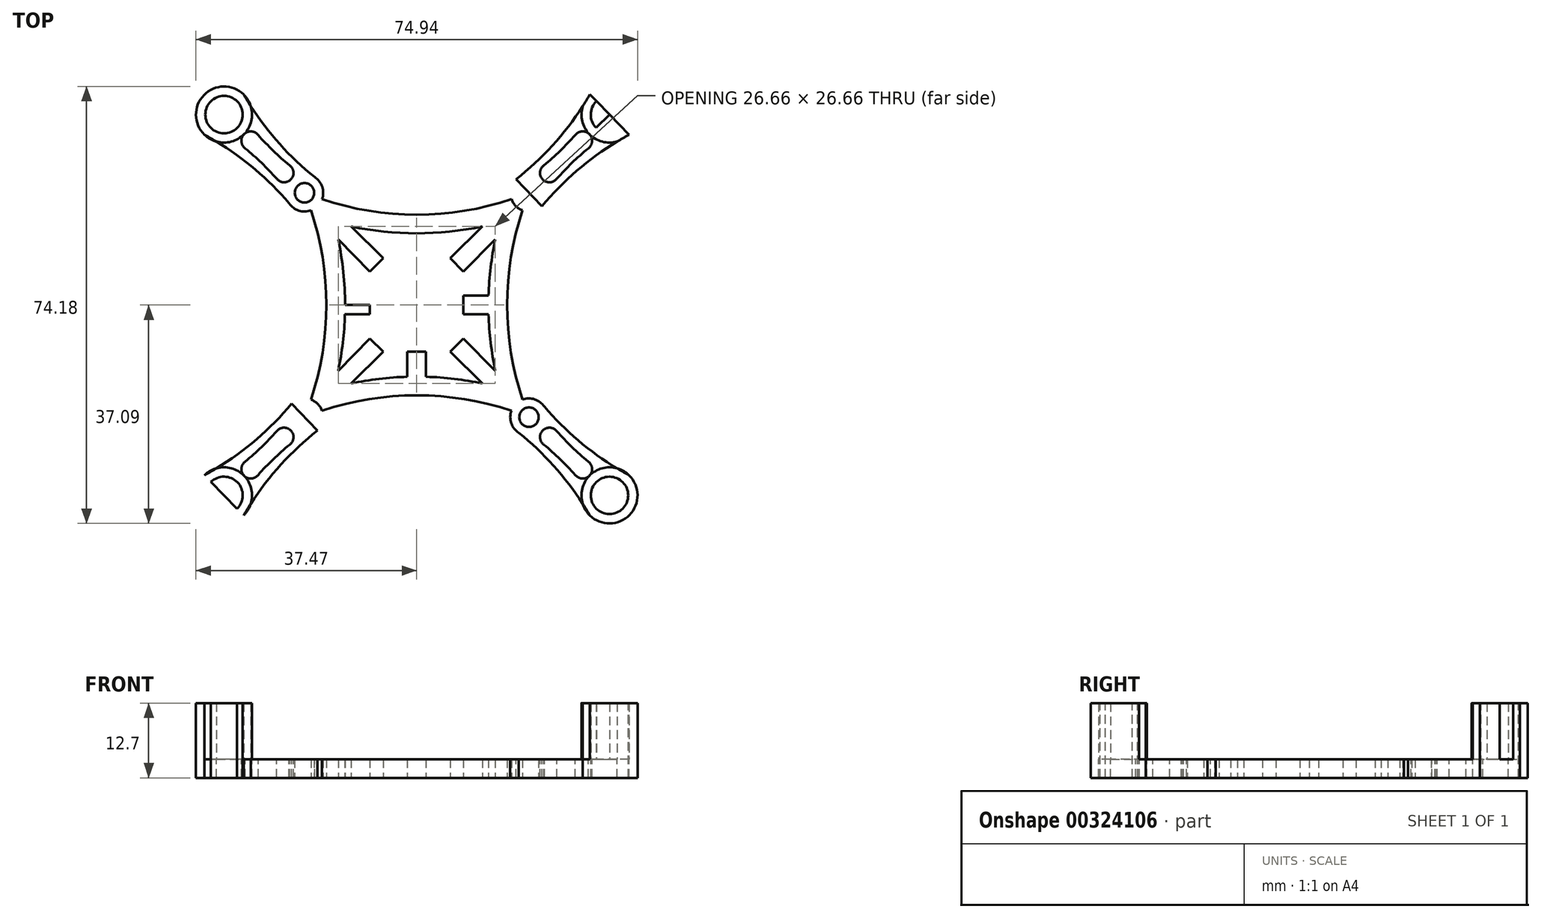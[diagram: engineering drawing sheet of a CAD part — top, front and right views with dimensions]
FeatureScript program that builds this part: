
annotation { "Feature Type Name" : "Feature", "Feature Type Description" : "" }
export const myFeature = defineFeature(function(context is Context, id is Id, definition is map)
    precondition{}
    {
        {
            var Q0;
            Q0=qCreatedBy(makeId("Top.planeOp"),FACE);
            var sketch = newSketch(context, id + "F0", { "sketchPlane" : qUnion([Q0])});
            skPoint(sketch, "E0.middle", {"position": v(0, 0) * mm});
            skLineSegment(sketch, "E1.bottom", {"start": v(-7.94, 7.94) * mm, "end": v(7.94, 7.94) * mm});
            skLineSegment(sketch, "E1.top", {"start": v(-7.94, -7.94) * mm, "end": v(7.94, -7.94) * mm});
            skLineSegment(sketch, "E1.left", {"start": v(-7.94, 7.94) * mm, "end": v(-7.94, -7.94) * mm});
            skLineSegment(sketch, "E1.right", {"start": v(7.94, 7.94) * mm, "end": v(7.94, -7.94) * mm});
            skCircle(sketch, "E2", {"center": v(-19.05, 19.05) * mm, "radius": 3.18 * mm});
            skCircle(sketch, "E3", {"center": v(-19.05, 19.05) * mm, "radius": 1.65 * mm});
            skCircle(sketch, "E4.MirrorC", {"center": v(19.05, 19.05) * mm, "radius": 3.18 * mm});
            skCircle(sketch, "E5.MirrorC", {"center": v(19.05, 19.05) * mm, "radius": 1.65 * mm});
            skCircle(sketch, "E6.MirrorC", {"center": v(-19.05, -19.05) * mm, "radius": 3.18 * mm});
            skCircle(sketch, "E7.MirrorC", {"center": v(-19.05, -19.05) * mm, "radius": 1.65 * mm});
            skCircle(sketch, "E8.MirrorC", {"center": v(19.05, -19.05) * mm, "radius": 3.18 * mm});
            skCircle(sketch, "E9.MirrorC", {"center": v(19.05, -19.05) * mm, "radius": 1.65 * mm});
            skArc(sketch, "E10", {"start": v(-19.05, 19.05) * mm, "mid": v(0, 15.34) * mm, "end": v(19.05, 19.05) * mm});
            skArc(sketch, "E11", {"start": v(19.05, 19.05) * mm, "mid": v(15.34, 0) * mm, "end": v(19.05, -19.05) * mm});
            skArc(sketch, "E12.MirrorCS", {"start": v(19.05, -19.05) * mm, "mid": v(15.34, 0) * mm, "end": v(19.05, 19.05) * mm});
            skArc(sketch, "E13.MirrorCS", {"start": v(19.05, 19.05) * mm, "mid": v(0, 15.34) * mm, "end": v(-19.05, 19.05) * mm});
            skArc(sketch, "E14.MirrorCS", {"start": v(-19.05, -19.05) * mm, "mid": v(-15.34, 0) * mm, "end": v(-19.05, 19.05) * mm});
            skArc(sketch, "E15.MirrorCS", {"start": v(19.05, -19.05) * mm, "mid": v(0, -15.34) * mm, "end": v(-19.05, -19.05) * mm});
            skArc(sketch, "E16.0", {"start": v(14.02, 14.02) * mm, "mid": v(0, 12.17) * mm, "end": v(-14.02, 14.02) * mm});
            skArc(sketch, "E16.1", {"start": v(14.02, 14.02) * mm, "mid": v(12.17, 0) * mm, "end": v(14.02, -14.02) * mm});
            skArc(sketch, "E16.2", {"start": v(14.02, -14.02) * mm, "mid": v(0, -12.17) * mm, "end": v(-14.02, -14.02) * mm});
            skArc(sketch, "E16.3", {"start": v(-14.02, -14.02) * mm, "mid": v(-12.17, 0) * mm, "end": v(-14.02, 14.02) * mm});
            skLineSegment(sketch, "E17.bottom", {"start": v(0, 7.94) * mm, "end": v(-1.59, 7.94) * mm});
            skLineSegment(sketch, "E17.top", {"start": v(0, 13.02) * mm, "end": v(-1.59, 13.02) * mm});
            skLineSegment(sketch, "E17.left", {"start": v(0, 7.94) * mm, "end": v(0, 13.02) * mm});
            skLineSegment(sketch, "E17.right", {"start": v(-1.59, 7.94) * mm, "end": v(-1.59, 13.02) * mm});
            skLineSegment(sketch, "E18.MirrorCS", {"start": v(-1.59, -7.94) * mm, "end": v(-1.59, -13.02) * mm});
            skLineSegment(sketch, "E19.MirrorCS", {"start": v(0, -7.94) * mm, "end": v(0, -13.02) * mm});
            skLineSegment(sketch, "E20.MirrorCS", {"start": v(0, -13.02) * mm, "end": v(-1.59, -13.02) * mm});
            skLineSegment(sketch, "E21.MirrorCS", {"start": v(0, -13.02) * mm, "end": v(1.59, -13.02) * mm});
            skLineSegment(sketch, "E22.MirrorCS", {"start": v(1.59, -7.94) * mm, "end": v(1.59, -13.02) * mm});
            skLineSegment(sketch, "E23.MirrorCS", {"start": v(7.94, -7.94) * mm, "end": v(-7.94, -7.94) * mm});
            skLineSegment(sketch, "E24.MirrorCS", {"start": v(1.59, 7.94) * mm, "end": v(1.59, 13.02) * mm});
            skLineSegment(sketch, "E25.MirrorCS", {"start": v(0, 13.02) * mm, "end": v(1.59, 13.02) * mm});
            skLineSegment(sketch, "E26.bottom", {"start": v(-7.94, 0) * mm, "end": v(-13.02, 0) * mm});
            skLineSegment(sketch, "E26.top", {"start": v(-7.94, 1.59) * mm, "end": v(-13.02, 1.59) * mm});
            skLineSegment(sketch, "E26.left", {"start": v(-7.94, 0) * mm, "end": v(-7.94, 1.59) * mm});
            skLineSegment(sketch, "E26.right", {"start": v(-13.02, 0) * mm, "end": v(-13.02, 1.59) * mm});
            skLineSegment(sketch, "E27.MirrorCS", {"start": v(7.94, 1.59) * mm, "end": v(13.02, 1.59) * mm});
            skLineSegment(sketch, "E28.MirrorCS", {"start": v(13.02, 0) * mm, "end": v(13.02, 1.59) * mm});
            skLineSegment(sketch, "E29.MirrorCS", {"start": v(7.94, 0) * mm, "end": v(13.02, 0) * mm});
            skLineSegment(sketch, "E30.MirrorCS", {"start": v(-13.02, 0) * mm, "end": v(-13.02, -1.59) * mm});
            skLineSegment(sketch, "E31.MirrorCS", {"start": v(-7.94, -1.59) * mm, "end": v(-13.02, -1.59) * mm});
            skLineSegment(sketch, "E32.MirrorCS", {"start": v(7.94, -1.59) * mm, "end": v(13.02, -1.59) * mm});
            skLineSegment(sketch, "E33.MirrorCS", {"start": v(13.02, 0) * mm, "end": v(13.02, -1.59) * mm});
            skLineSegment(sketch, "E34", {"start": v(-7.94, 5.7) * mm, "end": v(-5.7, 7.94) * mm});
            skLineSegment(sketch, "E35", {"start": v(-7.94, 7.94) * mm, "end": v(-6.81, 6.81) * mm});
            skLineSegment(sketch, "E36", {"start": v(-7.94, 5.7) * mm, "end": v(-13.33, 11.15) * mm});
            skLineSegment(sketch, "E37", {"start": v(-13.33, 11.15) * mm, "end": v(-11.13, 13.33) * mm});
            skLineSegment(sketch, "E38", {"start": v(-11.13, 13.33) * mm, "end": v(-5.7, 7.94) * mm});
            skLineSegment(sketch, "E39.MirrorCS", {"start": v(11.13, 13.33) * mm, "end": v(5.7, 7.94) * mm});
            skLineSegment(sketch, "E40.MirrorCS", {"start": v(7.94, 5.7) * mm, "end": v(5.7, 7.94) * mm});
            skLineSegment(sketch, "E41.MirrorCS", {"start": v(7.94, 5.7) * mm, "end": v(13.33, 11.15) * mm});
            skLineSegment(sketch, "E42.MirrorCS", {"start": v(13.33, 11.15) * mm, "end": v(11.13, 13.33) * mm});
            skLineSegment(sketch, "E43.MirrorCS", {"start": v(7.94, -5.7) * mm, "end": v(13.33, -11.15) * mm});
            skLineSegment(sketch, "E44.MirrorCS", {"start": v(7.94, -5.7) * mm, "end": v(5.7, -7.94) * mm});
            skLineSegment(sketch, "E45.MirrorCS", {"start": v(11.13, -13.33) * mm, "end": v(5.7, -7.94) * mm});
            skLineSegment(sketch, "E46.MirrorCS", {"start": v(-7.94, -5.7) * mm, "end": v(-5.7, -7.94) * mm});
            skLineSegment(sketch, "E47.MirrorCS", {"start": v(-11.13, -13.33) * mm, "end": v(-5.7, -7.94) * mm});
            skLineSegment(sketch, "E48.MirrorCS", {"start": v(-13.33, -11.15) * mm, "end": v(-11.13, -13.33) * mm});
            skLineSegment(sketch, "E49.MirrorCS", {"start": v(-7.94, -5.7) * mm, "end": v(-13.33, -11.15) * mm});
            skLineSegment(sketch, "E50.MirrorCS", {"start": v(13.33, -11.15) * mm, "end": v(11.13, -13.33) * mm});
            skLineSegment(sketch, "E51", {"start": v(19.05, -19.05) * mm, "end": v(16.8, -16.81) * mm});
            skPoint(sketch, "E52", {"position": v(17.08, -17.1) * mm});
            skLineSegment(sketch, "E53", {"start": v(17.08, -17.1) * mm, "end": v(17.64, -16.53) * mm});
            skLineSegment(sketch, "E54", {"start": v(17.64, -16.53) * mm, "end": v(16.5, -15.41) * mm});
            skLineSegment(sketch, "E55", {"start": v(16.5, -15.41) * mm, "end": v(15.95, -15.98) * mm});
            skLineSegment(sketch, "E56", {"start": v(15.95, -15.98) * mm, "end": v(16.8, -16.81) * mm});
            skLineSegment(sketch, "E57.MirrorCS", {"start": v(15.4, -16.54) * mm, "end": v(15.95, -15.98) * mm});
            skLineSegment(sketch, "E58.MirrorCS", {"start": v(16.52, -17.66) * mm, "end": v(15.4, -16.54) * mm});
            skLineSegment(sketch, "E59.MirrorCS", {"start": v(17.08, -17.1) * mm, "end": v(16.52, -17.66) * mm});
            skLineSegment(sketch, "E60", {"start": v(15.4, -16.54) * mm, "end": v(14.26, -15.42) * mm});
            skLineSegment(sketch, "E61", {"start": v(14.26, -15.42) * mm, "end": v(15.38, -14.3) * mm});
            skLineSegment(sketch, "E62", {"start": v(15.38, -14.3) * mm, "end": v(16.5, -15.41) * mm});
            skLineSegment(sketch, "E63", {"start": v(15.1, -16.26) * mm, "end": v(16.23, -15.13) * mm});
            skLineSegment(sketch, "E64.MirrorCS", {"start": v(-15.4, -16.54) * mm, "end": v(-14.26, -15.42) * mm});
            skLineSegment(sketch, "E65.MirrorCS", {"start": v(-15.1, -16.26) * mm, "end": v(-16.23, -15.13) * mm});
            skLineSegment(sketch, "E66.MirrorCS", {"start": v(-15.38, -14.3) * mm, "end": v(-16.5, -15.41) * mm});
            skLineSegment(sketch, "E67.MirrorCS", {"start": v(-14.26, -15.42) * mm, "end": v(-15.38, -14.3) * mm});
            skLineSegment(sketch, "E68.MirrorCS", {"start": v(15.38, 14.3) * mm, "end": v(16.5, 15.41) * mm});
            skLineSegment(sketch, "E69.MirrorCS", {"start": v(15.1, 16.26) * mm, "end": v(16.23, 15.13) * mm});
            skLineSegment(sketch, "E70.MirrorCS", {"start": v(15.4, 16.54) * mm, "end": v(14.26, 15.42) * mm});
            skLineSegment(sketch, "E71.MirrorCS", {"start": v(14.26, 15.42) * mm, "end": v(15.38, 14.3) * mm});
            skLineSegment(sketch, "E72.MirrorCS", {"start": v(-15.38, 14.3) * mm, "end": v(-16.5, 15.41) * mm});
            skLineSegment(sketch, "E73.MirrorCS", {"start": v(-15.4, 16.54) * mm, "end": v(-14.26, 15.42) * mm});
            skLineSegment(sketch, "E74.MirrorCS", {"start": v(-14.26, 15.42) * mm, "end": v(-15.38, 14.3) * mm});
            skLineSegment(sketch, "E75.MirrorCS", {"start": v(-15.1, 16.26) * mm, "end": v(-16.23, 15.13) * mm});
            skSolve(sketch);
        }
        {
            var Q0;
            {var subQ0=sQuery(id+"F0.wireOp",EDGE,"E13.MirrorCS");var subQ1=sQuery(id+"F0.wireOp",EDGE,"E2");var subQ2=makeQuery(id+"F0.imprint","INTERSECT",VERTEX,{"derivedFrom":[subQ1,subQ0]});Q0=makeQuery(id+"F0.imprint","IMPRINT",FACE,{"disambiguationData":[TD([[makeQuery(id+"F0.imprint","IMPRINT",EDGE,{"disambiguationData":[TD([[subQ2,-1.0]])],"derivedFrom":subQ1}),1.0]])]});}
            var Q1;
            {var subQ0=sQuery(id+"F0.wireOp",EDGE,"E13.MirrorCS");var subQ1=sQuery(id+"F0.wireOp",EDGE,"E2");var subQ2=makeQuery(id+"F0.imprint","INTERSECT",VERTEX,{"derivedFrom":[subQ1,subQ0]});Q1=makeQuery(id+"F0.imprint","IMPRINT",FACE,{"disambiguationData":[TD([[makeQuery(id+"F0.imprint","IMPRINT",EDGE,{"disambiguationData":[TD([[subQ2,1.0]])],"derivedFrom":subQ1}),1.0]])]});}
            var Q2;
            {var subQ26=sQuery(id+"F0.wireOp",EDGE,"E17.top");Q2=makeQuery(id+"F0.imprint","IMPRINT",FACE,{"disambiguationData":[TD([[makeQuery(id+"F0.imprint","IMPRINT",EDGE,{"derivedFrom":subQ26}),-1.0]])]});}
            var Q3;
            {var subQ0=sQuery(id+"F0.wireOp",EDGE,"E11");var subQ1=sQuery(id+"F0.wireOp",EDGE,"E4.MirrorC");var subQ2=makeQuery(id+"F0.imprint","INTERSECT",VERTEX,{"derivedFrom":[subQ1,subQ0]});Q3=makeQuery(id+"F0.imprint","IMPRINT",FACE,{"disambiguationData":[TD([[makeQuery(id+"F0.imprint","IMPRINT",EDGE,{"disambiguationData":[TD([[subQ2,-1.0]])],"derivedFrom":subQ1}),-1.0]])]});}
            var Q4;
            {var subQ0=sQuery(id+"F0.wireOp",EDGE,"E11");var subQ1=sQuery(id+"F0.wireOp",EDGE,"E4.MirrorC");var subQ2=makeQuery(id+"F0.imprint","INTERSECT",VERTEX,{"derivedFrom":[subQ1,subQ0]});Q4=makeQuery(id+"F0.imprint","IMPRINT",FACE,{"disambiguationData":[TD([[makeQuery(id+"F0.imprint","IMPRINT",EDGE,{"disambiguationData":[TD([[subQ2,1.0]])],"derivedFrom":subQ1}),-1.0]])]});}
            var Q5;
            {var subQ5=sQuery(id+"F0.wireOp",EDGE,"E17.top");Q5=makeQuery(id+"F0.imprint","IMPRINT",FACE,{"disambiguationData":[TD([[makeQuery(id+"F0.imprint","IMPRINT",EDGE,{"derivedFrom":subQ5}),1.0]])]});}
            var Q6;
            {var subQ3=sQuery(id+"F0.wireOp",EDGE,"E37");Q6=makeQuery(id+"F0.imprint","IMPRINT",FACE,{"disambiguationData":[TD([[makeQuery(id+"F0.imprint","IMPRINT",EDGE,{"derivedFrom":subQ3}),1.0]])]});}
            var Q7;
            {var subQ5=sQuery(id+"F0.wireOp",EDGE,"E25.MirrorCS");Q7=makeQuery(id+"F0.imprint","IMPRINT",FACE,{"disambiguationData":[TD([[makeQuery(id+"F0.imprint","IMPRINT",EDGE,{"derivedFrom":subQ5}),-1.0]])]});}
            var Q8;
            {var subQ3=sQuery(id+"F0.wireOp",EDGE,"E42.MirrorCS");Q8=makeQuery(id+"F0.imprint","IMPRINT",FACE,{"disambiguationData":[TD([[makeQuery(id+"F0.imprint","IMPRINT",EDGE,{"derivedFrom":subQ3}),-1.0]])]});}
            var Q9;
            {var subQ1=sQuery(id+"F0.wireOp",EDGE,"E39.MirrorCS");Q9=makeQuery(id+"F0.imprint","IMPRINT",FACE,{"disambiguationData":[TD([[makeQuery(id+"F0.imprint","IMPRINT",EDGE,{"derivedFrom":subQ1}),1.0]])]});}
            var Q10;
            {var subQ5=sQuery(id+"F0.wireOp",EDGE,"E36");Q10=makeQuery(id+"F0.imprint","IMPRINT",FACE,{"disambiguationData":[TD([[makeQuery(id+"F0.imprint","IMPRINT",EDGE,{"derivedFrom":subQ5}),-1.0]])]});}
            var Q11;
            {var subQ5=sQuery(id+"F0.wireOp",EDGE,"E17.bottom");Q11=makeQuery(id+"F0.imprint","IMPRINT",FACE,{"disambiguationData":[TD([[makeQuery(id+"F0.imprint","IMPRINT",EDGE,{"derivedFrom":subQ5}),-1.0]])]});}
            var Q12;
            {var subQ3=sQuery(id+"F0.wireOp",EDGE,"E24.MirrorCS");var subQ5=sQuery(id+"F0.wireOp",EDGE,"E16.0");var subQ6=makeQuery(id+"F0.imprint","INTERSECT",VERTEX,{"derivedFrom":[subQ5,subQ3]});Q12=makeQuery(id+"F0.imprint","IMPRINT",FACE,{"disambiguationData":[TD([[makeQuery(id+"F0.imprint","IMPRINT",EDGE,{"disambiguationData":[TD([[subQ6,-1.0]])],"derivedFrom":subQ5}),1.0]])]});}
            var Q13;
            {var subQ0=sQuery(id+"F0.wireOp",EDGE,"E35");Q13=makeQuery(id+"F0.imprint","IMPRINT",FACE,{"disambiguationData":[TD([[makeQuery(id+"F0.imprint","IMPRINT",EDGE,{"derivedFrom":subQ0}),1.0]])]});}
            var Q14;
            {var subQ0=sQuery(id+"F0.wireOp",EDGE,"E35");Q14=makeQuery(id+"F0.imprint","IMPRINT",FACE,{"disambiguationData":[TD([[makeQuery(id+"F0.imprint","IMPRINT",EDGE,{"derivedFrom":subQ0}),-1.0]])]});}
            var Q15;
            {var subQ3=sQuery(id+"F0.wireOp",EDGE,"E40.MirrorCS");Q15=makeQuery(id+"F0.imprint","IMPRINT",FACE,{"disambiguationData":[TD([[makeQuery(id+"F0.imprint","IMPRINT",EDGE,{"derivedFrom":subQ3}),-1.0]])]});}
            var Q16;
            {var subQ12=sQuery(id+"F0.wireOp",EDGE,"E17.bottom");Q16=makeQuery(id+"F0.imprint","IMPRINT",FACE,{"disambiguationData":[TD([[makeQuery(id+"F0.imprint","IMPRINT",EDGE,{"derivedFrom":subQ12}),1.0]])]});}
            var Q17;
            {var subQ5=sQuery(id+"F0.wireOp",EDGE,"E26.right");Q17=makeQuery(id+"F0.imprint","IMPRINT",FACE,{"disambiguationData":[TD([[makeQuery(id+"F0.imprint","IMPRINT",EDGE,{"derivedFrom":subQ5}),-1.0]])]});}
            var Q18;
            {var subQ5=sQuery(id+"F0.wireOp",EDGE,"E30.MirrorCS");Q18=makeQuery(id+"F0.imprint","IMPRINT",FACE,{"disambiguationData":[TD([[makeQuery(id+"F0.imprint","IMPRINT",EDGE,{"derivedFrom":subQ5}),1.0]])]});}
            var Q19;
            {var subQ3=sQuery(id+"F0.wireOp",EDGE,"E31.MirrorCS");var subQ5=sQuery(id+"F0.wireOp",EDGE,"E16.3");var subQ6=makeQuery(id+"F0.imprint","INTERSECT",VERTEX,{"derivedFrom":[subQ5,subQ3]});Q19=makeQuery(id+"F0.imprint","IMPRINT",FACE,{"disambiguationData":[TD([[makeQuery(id+"F0.imprint","IMPRINT",EDGE,{"disambiguationData":[TD([[subQ6,-1.0]])],"derivedFrom":subQ5}),-1.0]])]});}
            var Q20;
            {var subQ5=sQuery(id+"F0.wireOp",EDGE,"E26.left");Q20=makeQuery(id+"F0.imprint","IMPRINT",FACE,{"disambiguationData":[TD([[makeQuery(id+"F0.imprint","IMPRINT",EDGE,{"derivedFrom":subQ5}),1.0]])]});}
            var Q21;
            {var subQ5=sQuery(id+"F0.wireOp",EDGE,"E28.MirrorCS");Q21=makeQuery(id+"F0.imprint","IMPRINT",FACE,{"disambiguationData":[TD([[makeQuery(id+"F0.imprint","IMPRINT",EDGE,{"derivedFrom":subQ5}),1.0]])]});}
            var Q22;
            {var subQ5=sQuery(id+"F0.wireOp",EDGE,"E33.MirrorCS");Q22=makeQuery(id+"F0.imprint","IMPRINT",FACE,{"disambiguationData":[TD([[makeQuery(id+"F0.imprint","IMPRINT",EDGE,{"derivedFrom":subQ5}),-1.0]])]});}
            var Q23;
            {var subQ3=sQuery(id+"F0.wireOp",EDGE,"E46.MirrorCS");Q23=makeQuery(id+"F0.imprint","IMPRINT",FACE,{"disambiguationData":[TD([[makeQuery(id+"F0.imprint","IMPRINT",EDGE,{"derivedFrom":subQ3}),-1.0]])]});}
            var Q24;
            {var subQ3=sQuery(id+"F0.wireOp",EDGE,"E48.MirrorCS");Q24=makeQuery(id+"F0.imprint","IMPRINT",FACE,{"disambiguationData":[TD([[makeQuery(id+"F0.imprint","IMPRINT",EDGE,{"derivedFrom":subQ3}),-1.0]])]});}
            var Q25;
            {var subQ0=sQuery(id+"F0.wireOp",EDGE,"E14.MirrorCS");var subQ1=sQuery(id+"F0.wireOp",EDGE,"E6.MirrorC");var subQ2=makeQuery(id+"F0.imprint","INTERSECT",VERTEX,{"derivedFrom":[subQ1,subQ0]});Q25=makeQuery(id+"F0.imprint","IMPRINT",FACE,{"disambiguationData":[TD([[makeQuery(id+"F0.imprint","IMPRINT",EDGE,{"disambiguationData":[TD([[subQ2,-1.0]])],"derivedFrom":subQ1}),-1.0]])]});}
            var Q26;
            {var subQ0=sQuery(id+"F0.wireOp",EDGE,"E14.MirrorCS");var subQ1=sQuery(id+"F0.wireOp",EDGE,"E6.MirrorC");var subQ2=makeQuery(id+"F0.imprint","INTERSECT",VERTEX,{"derivedFrom":[subQ1,subQ0]});Q26=makeQuery(id+"F0.imprint","IMPRINT",FACE,{"disambiguationData":[TD([[makeQuery(id+"F0.imprint","IMPRINT",EDGE,{"disambiguationData":[TD([[subQ2,1.0]])],"derivedFrom":subQ1}),-1.0]])]});}
            var Q27;
            {var subQ5=sQuery(id+"F0.wireOp",EDGE,"E20.MirrorCS");Q27=makeQuery(id+"F0.imprint","IMPRINT",FACE,{"disambiguationData":[TD([[makeQuery(id+"F0.imprint","IMPRINT",EDGE,{"derivedFrom":subQ5}),-1.0]])]});}
            var Q28;
            {var subQ5=sQuery(id+"F0.wireOp",EDGE,"E21.MirrorCS");Q28=makeQuery(id+"F0.imprint","IMPRINT",FACE,{"disambiguationData":[TD([[makeQuery(id+"F0.imprint","IMPRINT",EDGE,{"derivedFrom":subQ5}),1.0]])]});}
            var Q29;
            {var subQ0=sQuery(id+"F0.wireOp",EDGE,"E11");var subQ1=sQuery(id+"F0.wireOp",EDGE,"E8.MirrorC");var subQ2=makeQuery(id+"F0.imprint","INTERSECT",VERTEX,{"derivedFrom":[subQ1,subQ0]});Q29=makeQuery(id+"F0.imprint","IMPRINT",FACE,{"disambiguationData":[TD([[makeQuery(id+"F0.imprint","IMPRINT",EDGE,{"disambiguationData":[TD([[subQ2,1.0]])],"derivedFrom":subQ1}),1.0]])]});}
            var Q30;
            {var subQ0=sQuery(id+"F0.wireOp",EDGE,"E11");var subQ1=sQuery(id+"F0.wireOp",EDGE,"E8.MirrorC");var subQ2=makeQuery(id+"F0.imprint","INTERSECT",VERTEX,{"derivedFrom":[subQ1,subQ0]});Q30=makeQuery(id+"F0.imprint","IMPRINT",FACE,{"disambiguationData":[TD([[makeQuery(id+"F0.imprint","IMPRINT",EDGE,{"disambiguationData":[TD([[subQ2,-1.0]])],"derivedFrom":subQ1}),1.0]])]});}
            var Q31;
            {var subQ0=sQuery(id+"F0.wireOp",EDGE,"E29.MirrorCS");var subQ1=sQuery(id+"F0.wireOp",EDGE,"E1.right");var subQ2=makeQuery(id+"F0.imprint","INTERSECT",VERTEX,{"derivedFrom":[subQ1,subQ0]});Q31=makeQuery(id+"F0.imprint","IMPRINT",FACE,{"disambiguationData":[TD([[makeQuery(id+"F0.imprint","IMPRINT",EDGE,{"disambiguationData":[TD([[subQ2,-1.0]])],"derivedFrom":subQ1}),1.0]])]});}
            var Q32;
            {var subQ0=sQuery(id+"F0.wireOp",EDGE,"E27.MirrorCS");var subQ1=sQuery(id+"F0.wireOp",EDGE,"E1.right");var subQ2=makeQuery(id+"F0.imprint","INTERSECT",VERTEX,{"derivedFrom":[subQ1,subQ0]});Q32=makeQuery(id+"F0.imprint","IMPRINT",FACE,{"disambiguationData":[TD([[makeQuery(id+"F0.imprint","IMPRINT",EDGE,{"disambiguationData":[TD([[subQ2,-1.0]])],"derivedFrom":subQ1}),1.0]])]});}
            var Q33;
            {var subQ0=sQuery(id+"F0.wireOp",EDGE,"E47.MirrorCS");Q33=makeQuery(id+"F0.imprint","IMPRINT",FACE,{"disambiguationData":[TD([[makeQuery(id+"F0.imprint","IMPRINT",EDGE,{"derivedFrom":subQ0}),1.0]])]});}
            var Q34;
            {var subQ3=sQuery(id+"F0.wireOp",EDGE,"E44.MirrorCS");Q34=makeQuery(id+"F0.imprint","IMPRINT",FACE,{"disambiguationData":[TD([[makeQuery(id+"F0.imprint","IMPRINT",EDGE,{"derivedFrom":subQ3}),1.0]])]});}
            var Q35;
            {var subQ3=sQuery(id+"F0.wireOp",EDGE,"E50.MirrorCS");Q35=makeQuery(id+"F0.imprint","IMPRINT",FACE,{"disambiguationData":[TD([[makeQuery(id+"F0.imprint","IMPRINT",EDGE,{"derivedFrom":subQ3}),1.0]])]});}
            var Q36;
            {var subQ1=sQuery(id+"F0.wireOp",EDGE,"E43.MirrorCS");Q36=makeQuery(id+"F0.imprint","IMPRINT",FACE,{"disambiguationData":[TD([[makeQuery(id+"F0.imprint","IMPRINT",EDGE,{"derivedFrom":subQ1}),-1.0]])]});}
            var Q37;
            {var subQ0=sQuery(id+"F0.wireOp",EDGE,"E22.MirrorCS");var subQ1=sQuery(id+"F0.wireOp",EDGE,"E16.2");var subQ2=makeQuery(id+"F0.imprint","INTERSECT",VERTEX,{"derivedFrom":[subQ1,subQ0]});Q37=makeQuery(id+"F0.imprint","IMPRINT",FACE,{"disambiguationData":[TD([[makeQuery(id+"F0.imprint","IMPRINT",EDGE,{"disambiguationData":[TD([[subQ2,-1.0]])],"derivedFrom":subQ1}),-1.0]])]});}
            var Q38;
            {var subQ0=sQuery(id+"F0.wireOp",EDGE,"E19.MirrorCS");var subQ1=sQuery(id+"F0.wireOp",EDGE,"E16.2");var subQ2=makeQuery(id+"F0.imprint","INTERSECT",VERTEX,{"derivedFrom":[subQ1,subQ0]});Q38=makeQuery(id+"F0.imprint","IMPRINT",FACE,{"disambiguationData":[TD([[makeQuery(id+"F0.imprint","IMPRINT",EDGE,{"disambiguationData":[TD([[subQ2,-1.0]])],"derivedFrom":subQ1}),-1.0]])]});}
            var Q39;
            {var subQ5=sQuery(id+"F0.wireOp",EDGE,"E59.MirrorCS");Q39=makeQuery(id+"F0.imprint","IMPRINT",FACE,{"disambiguationData":[TD([[makeQuery(id+"F0.imprint","IMPRINT",EDGE,{"derivedFrom":subQ5}),1.0]])]});}
            var Q40;
            {var subQ0=sQuery(id+"F0.wireOp",EDGE,"E56");Q40=makeQuery(id+"F0.imprint","IMPRINT",FACE,{"disambiguationData":[TD([[makeQuery(id+"F0.imprint","IMPRINT",EDGE,{"derivedFrom":subQ0}),-1.0]])]});}
            var Q41;
            {var subQ5=sQuery(id+"F0.wireOp",EDGE,"E59.MirrorCS");Q41=makeQuery(id+"F0.imprint","IMPRINT",FACE,{"disambiguationData":[TD([[makeQuery(id+"F0.imprint","IMPRINT",EDGE,{"derivedFrom":subQ5}),-1.0]])]});}
            var Q42;
            {var subQ5=sQuery(id+"F0.wireOp",EDGE,"E53");Q42=makeQuery(id+"F0.imprint","IMPRINT",FACE,{"disambiguationData":[TD([[makeQuery(id+"F0.imprint","IMPRINT",EDGE,{"derivedFrom":subQ5}),1.0]])]});}
            var Q43;
            {var subQ4=sQuery(id+"F0.wireOp",EDGE,"E55");Q43=makeQuery(id+"F0.imprint","IMPRINT",FACE,{"disambiguationData":[TD([[makeQuery(id+"F0.imprint","IMPRINT",EDGE,{"derivedFrom":subQ4}),1.0]])]});}
            var Q44;
            {var subQ1=sQuery(id+"F0.wireOp",EDGE,"E55");Q44=makeQuery(id+"F0.imprint","IMPRINT",FACE,{"disambiguationData":[TD([[makeQuery(id+"F0.imprint","IMPRINT",EDGE,{"derivedFrom":subQ1}),-1.0]])]});}
            var Q45;
            {var subQ2=sQuery(id+"F0.wireOp",EDGE,"E69.MirrorCS");Q45=makeQuery(id+"F0.imprint","IMPRINT",FACE,{"disambiguationData":[TD([[makeQuery(id+"F0.imprint","IMPRINT",EDGE,{"derivedFrom":subQ2}),-1.0]])]});}
            var Q46;
            {var subQ0=sQuery(id+"F0.wireOp",EDGE,"E61");Q46=makeQuery(id+"F0.imprint","IMPRINT",FACE,{"disambiguationData":[TD([[makeQuery(id+"F0.imprint","IMPRINT",EDGE,{"derivedFrom":subQ0}),-1.0]])]});}
            var Q47;
            {var subQ2=sQuery(id+"F0.wireOp",EDGE,"E65.MirrorCS");Q47=makeQuery(id+"F0.imprint","IMPRINT",FACE,{"disambiguationData":[TD([[makeQuery(id+"F0.imprint","IMPRINT",EDGE,{"derivedFrom":subQ2}),-1.0]])]});}
            var Q48;
            {var subQ0=sQuery(id+"F0.wireOp",EDGE,"E74.MirrorCS");Q48=makeQuery(id+"F0.imprint","IMPRINT",FACE,{"disambiguationData":[TD([[makeQuery(id+"F0.imprint","IMPRINT",EDGE,{"derivedFrom":subQ0}),-1.0]])]});}
            extrude(context, id + "F1", {"entities" : qUnion([Q0, Q1, Q2, Q3, Q4, Q5, Q6, Q7, Q8, Q9, Q10, Q11, Q12, Q13, Q14, Q15, Q16, Q17, Q18, Q19, Q20, Q21, Q22, Q23, Q24, Q25, Q26, Q27, Q28, Q29, Q30, Q31, Q32, Q33, Q34, Q35, Q36, Q37, Q38, Q39, Q40, Q41, Q42, Q43, Q44, Q45, Q46, Q47, Q48]), "depth" : 3.17 * mm});
        }
        {
            var Q0;
            Q0=makeQuery(id+"F1.opExtrude","CAP_FACE",FACE,{"disambiguationData":[OSD([sQuery(id+"F0.wireOp",EDGE,"E1.bottom"),sQuery(id+"F0.wireOp",EDGE,"E1.left"),sQuery(id+"F0.wireOp",EDGE,"E1.right"),sQuery(id+"F0.wireOp",EDGE,"E2"),sQuery(id+"F0.wireOp",EDGE,"E3"),sQuery(id+"F0.wireOp",EDGE,"E4.MirrorC"),sQuery(id+"F0.wireOp",EDGE,"E5.MirrorC"),sQuery(id+"F0.wireOp",EDGE,"E6.MirrorC"),sQuery(id+"F0.wireOp",EDGE,"E7.MirrorC"),sQuery(id+"F0.wireOp",EDGE,"E8.MirrorC"),sQuery(id+"F0.wireOp",EDGE,"E9.MirrorC"),sQuery(id+"F0.wireOp",EDGE,"E11"),sQuery(id+"F0.wireOp",EDGE,"E13.MirrorCS"),sQuery(id+"F0.wireOp",EDGE,"E14.MirrorCS"),sQuery(id+"F0.wireOp",EDGE,"E15.MirrorCS"),sQuery(id+"F0.wireOp",EDGE,"E16.0"),sQuery(id+"F0.wireOp",EDGE,"E16.1"),sQuery(id+"F0.wireOp",EDGE,"E16.2"),sQuery(id+"F0.wireOp",EDGE,"E16.3"),sQuery(id+"F0.wireOp",EDGE,"E17.right"),sQuery(id+"F0.wireOp",EDGE,"E18.MirrorCS"),sQuery(id+"F0.wireOp",EDGE,"E22.MirrorCS"),sQuery(id+"F0.wireOp",EDGE,"E23.MirrorCS"),sQuery(id+"F0.wireOp",EDGE,"E24.MirrorCS"),sQuery(id+"F0.wireOp",EDGE,"E26.top"),sQuery(id+"F0.wireOp",EDGE,"E27.MirrorCS"),sQuery(id+"F0.wireOp",EDGE,"E31.MirrorCS"),sQuery(id+"F0.wireOp",EDGE,"E32.MirrorCS"),sQuery(id+"F0.wireOp",EDGE,"E36"),sQuery(id+"F0.wireOp",EDGE,"E38"),sQuery(id+"F0.wireOp",EDGE,"E39.MirrorCS"),sQuery(id+"F0.wireOp",EDGE,"E41.MirrorCS"),sQuery(id+"F0.wireOp",EDGE,"E43.MirrorCS"),sQuery(id+"F0.wireOp",EDGE,"E45.MirrorCS"),sQuery(id+"F0.wireOp",EDGE,"E47.MirrorCS"),sQuery(id+"F0.wireOp",EDGE,"E49.MirrorCS")])],"isStart":false});
            var sketch = newSketch(context, id + "F2", { "sketchPlane" : qUnion([Q0])});
            skPoint(sketch, "E76", {"position": v(19.05, -19.05) * mm});
            skLineSegment(sketch, "E77", {"start": v(19.05, -19.05) * mm, "end": v(32.7, -32.33) * mm});
            skLineSegment(sketch, "E78", {"start": v(19.05, -19.05) * mm, "end": v(19.05, -15.88) * mm});
            skCircle(sketch, "E79", {"center": v(32.7, -32.33) * mm, "radius": 4.76 * mm});
            skCircle(sketch, "E80", {"center": v(32.7, -32.33) * mm, "radius": 3.18 * mm});
            skLineSegment(sketch, "E81", {"start": v(32.7, -32.33) * mm, "end": v(29.39, -35.74) * mm});
            skLineSegment(sketch, "E82", {"start": v(32.7, -32.33) * mm, "end": v(36.03, -28.92) * mm});
            skLineSegment(sketch, "E83", {"start": v(19.05, -19.05) * mm, "end": v(21.26, -16.77) * mm});
            skLineSegment(sketch, "E84", {"start": v(19.05, -19.05) * mm, "end": v(16.84, -21.33) * mm});
            skArc(sketch, "E85", {"start": v(29.39, -35.74) * mm, "mid": v(23.8, -27.94) * mm, "end": v(16.84, -21.33) * mm});
            skArc(sketch, "E86", {"start": v(21.26, -16.77) * mm, "mid": v(28.07, -23.55) * mm, "end": v(36.03, -28.92) * mm});
            skLineSegment(sketch, "E87.MirrorCS", {"start": v(-19.05, -19.05) * mm, "end": v(-16.84, -21.33) * mm});
            skLineSegment(sketch, "E88.MirrorCS", {"start": v(-19.05, -19.05) * mm, "end": v(-21.26, -16.77) * mm});
            skLineSegment(sketch, "E89.MirrorCS", {"start": v(-19.05, -19.05) * mm, "end": v(-19.05, -15.88) * mm});
            skCircle(sketch, "E90.MirrorC", {"center": v(-32.7, -32.33) * mm, "radius": 3.18 * mm});
            skLineSegment(sketch, "E91.MirrorCS", {"start": v(-32.7, -32.33) * mm, "end": v(-29.39, -35.74) * mm});
            skLineSegment(sketch, "E92.MirrorCS", {"start": v(-32.7, -32.33) * mm, "end": v(-36.03, -28.92) * mm});
            skArc(sketch, "E93.MirrorCS", {"start": v(-21.26, -16.77) * mm, "mid": v(-28.07, -23.55) * mm, "end": v(-36.03, -28.92) * mm});
            skArc(sketch, "E94.MirrorCS", {"start": v(-29.39, -35.74) * mm, "mid": v(-23.8, -27.94) * mm, "end": v(-16.84, -21.33) * mm});
            skPoint(sketch, "E95.MirrorP", {"position": v(-19.05, -19.05) * mm});
            skLineSegment(sketch, "E96.MirrorCS", {"start": v(-19.05, -19.05) * mm, "end": v(-32.7, -32.33) * mm});
            skCircle(sketch, "E97.MirrorC", {"center": v(-32.7, -32.33) * mm, "radius": 4.76 * mm});
            skLineSegment(sketch, "E98.MirrorCS", {"start": v(-19.05, 19.05) * mm, "end": v(-16.84, 21.33) * mm});
            skLineSegment(sketch, "E99.MirrorCS", {"start": v(-32.7, 32.33) * mm, "end": v(-29.39, 35.74) * mm});
            skLineSegment(sketch, "E100.MirrorCS", {"start": v(19.05, 19.05) * mm, "end": v(21.26, 16.77) * mm});
            skLineSegment(sketch, "E101.MirrorCS", {"start": v(19.05, 19.05) * mm, "end": v(16.84, 21.33) * mm});
            skLineSegment(sketch, "E102.MirrorCS", {"start": v(-19.05, 19.05) * mm, "end": v(-21.26, 16.77) * mm});
            skLineSegment(sketch, "E103.MirrorCS", {"start": v(32.7, 32.33) * mm, "end": v(36.03, 28.92) * mm});
            skLineSegment(sketch, "E104.MirrorCS", {"start": v(32.7, 32.33) * mm, "end": v(29.39, 35.74) * mm});
            skLineSegment(sketch, "E105.MirrorCS", {"start": v(19.05, 19.05) * mm, "end": v(19.05, 15.88) * mm});
            skLineSegment(sketch, "E106.MirrorCS", {"start": v(-32.7, 32.33) * mm, "end": v(-36.03, 28.92) * mm});
            skLineSegment(sketch, "E107.MirrorCS", {"start": v(-19.05, 19.05) * mm, "end": v(-19.05, 15.88) * mm});
            skLineSegment(sketch, "E108.MirrorCS", {"start": v(19.05, 19.05) * mm, "end": v(32.7, 32.33) * mm});
            skPoint(sketch, "E109.MirrorP", {"position": v(-19.05, 19.05) * mm});
            skArc(sketch, "E110.MirrorCS", {"start": v(-29.39, 35.74) * mm, "mid": v(-23.8, 27.94) * mm, "end": v(-16.84, 21.33) * mm});
            skPoint(sketch, "E111.MirrorP", {"position": v(19.05, 19.05) * mm});
            skLineSegment(sketch, "E112.MirrorCS", {"start": v(-19.05, 19.05) * mm, "end": v(-32.7, 32.33) * mm});
            skCircle(sketch, "E113.MirrorC", {"center": v(-32.7, 32.33) * mm, "radius": 4.76 * mm});
            skCircle(sketch, "E114.MirrorC", {"center": v(32.7, 32.33) * mm, "radius": 3.18 * mm});
            skCircle(sketch, "E115.MirrorC", {"center": v(32.7, 32.33) * mm, "radius": 4.76 * mm});
            skCircle(sketch, "E116.MirrorC", {"center": v(-32.7, 32.33) * mm, "radius": 3.18 * mm});
            skArc(sketch, "E117.MirrorCS", {"start": v(-21.26, 16.77) * mm, "mid": v(-28.07, 23.55) * mm, "end": v(-36.03, 28.92) * mm});
            skArc(sketch, "E118.MirrorCS", {"start": v(29.39, 35.74) * mm, "mid": v(23.8, 27.94) * mm, "end": v(16.84, 21.33) * mm});
            skArc(sketch, "E119.MirrorCS", {"start": v(21.26, 16.77) * mm, "mid": v(28.07, 23.55) * mm, "end": v(36.03, 28.92) * mm});
            skSolve(sketch);
        }
        {
            var Q0;
            {var subQ0=sQuery(id+"F2.wireOp",EDGE,"E86");var subQ1=sQuery(id+"F2.wireOp",EDGE,"E79");var subQ3=makeQuery(id+"F2.imprint","INTERSECT",VERTEX,{"derivedFrom":[subQ1,subQ0]});Q0=makeQuery(id+"F2.imprint","IMPRINT",FACE,{"disambiguationData":[TD([[makeQuery(id+"F2.imprint","IMPRINT",EDGE,{"disambiguationData":[TD([[subQ3,1.0]])],"derivedFrom":subQ1}),1.0]])]});}
            var Q1;
            {var subQ0=sQuery(id+"F2.wireOp",EDGE,"E85");var subQ1=sQuery(id+"F2.wireOp",EDGE,"E79");var subQ3=makeQuery(id+"F2.imprint","INTERSECT",VERTEX,{"derivedFrom":[subQ1,subQ0]});Q1=makeQuery(id+"F2.imprint","IMPRINT",FACE,{"disambiguationData":[TD([[makeQuery(id+"F2.imprint","IMPRINT",EDGE,{"disambiguationData":[TD([[subQ3,-1.0]])],"derivedFrom":subQ1}),1.0]])]});}
            var Q2;
            {var subQ0=sQuery(id+"F2.wireOp",EDGE,"E97.MirrorC");var subQ1=sQuery(id+"F2.wireOp",EDGE,"E93.MirrorCS");var subQ3=makeQuery(id+"F2.imprint","INTERSECT",VERTEX,{"derivedFrom":[subQ1,subQ0]});Q2=makeQuery(id+"F2.imprint","IMPRINT",FACE,{"disambiguationData":[TD([[makeQuery(id+"F2.imprint","IMPRINT",EDGE,{"disambiguationData":[TD([[subQ3,-1.0]])],"derivedFrom":subQ1}),-1.0]])]});}
            var Q3;
            {var subQ0=sQuery(id+"F2.wireOp",EDGE,"E97.MirrorC");var subQ1=sQuery(id+"F2.wireOp",EDGE,"E94.MirrorCS");var subQ3=makeQuery(id+"F2.imprint","INTERSECT",VERTEX,{"derivedFrom":[subQ1,subQ0]});Q3=makeQuery(id+"F2.imprint","IMPRINT",FACE,{"disambiguationData":[TD([[makeQuery(id+"F2.imprint","IMPRINT",EDGE,{"disambiguationData":[TD([[subQ3,1.0]])],"derivedFrom":subQ1}),-1.0]])]});}
            var Q4;
            {var subQ0=sQuery(id+"F2.wireOp",EDGE,"E113.MirrorC");var subQ1=sQuery(id+"F2.wireOp",EDGE,"E110.MirrorCS");var subQ3=makeQuery(id+"F2.imprint","INTERSECT",VERTEX,{"derivedFrom":[subQ1,subQ0]});Q4=makeQuery(id+"F2.imprint","IMPRINT",FACE,{"disambiguationData":[TD([[makeQuery(id+"F2.imprint","IMPRINT",EDGE,{"disambiguationData":[TD([[subQ3,1.0]])],"derivedFrom":subQ1}),1.0]])]});}
            var Q5;
            {var subQ0=sQuery(id+"F2.wireOp",EDGE,"E117.MirrorCS");var subQ1=sQuery(id+"F2.wireOp",EDGE,"E113.MirrorC");var subQ3=makeQuery(id+"F2.imprint","INTERSECT",VERTEX,{"derivedFrom":[subQ1,subQ0]});Q5=makeQuery(id+"F2.imprint","IMPRINT",FACE,{"disambiguationData":[TD([[makeQuery(id+"F2.imprint","IMPRINT",EDGE,{"disambiguationData":[TD([[subQ3,1.0]])],"derivedFrom":subQ1}),1.0]])]});}
            var Q6;
            {var subQ0=sQuery(id+"F2.wireOp",EDGE,"E119.MirrorCS");var subQ1=sQuery(id+"F2.wireOp",EDGE,"E115.MirrorC");var subQ3=makeQuery(id+"F2.imprint","INTERSECT",VERTEX,{"derivedFrom":[subQ1,subQ0]});Q6=makeQuery(id+"F2.imprint","IMPRINT",FACE,{"disambiguationData":[TD([[makeQuery(id+"F2.imprint","IMPRINT",EDGE,{"disambiguationData":[TD([[subQ3,1.0]])],"derivedFrom":subQ1}),-1.0]])]});}
            var Q7;
            {var subQ0=sQuery(id+"F2.wireOp",EDGE,"E118.MirrorCS");var subQ1=sQuery(id+"F2.wireOp",EDGE,"E115.MirrorC");var subQ3=makeQuery(id+"F2.imprint","INTERSECT",VERTEX,{"derivedFrom":[subQ1,subQ0]});Q7=makeQuery(id+"F2.imprint","IMPRINT",FACE,{"disambiguationData":[TD([[makeQuery(id+"F2.imprint","IMPRINT",EDGE,{"disambiguationData":[TD([[subQ3,-1.0]])],"derivedFrom":subQ1}),-1.0]])]});}
            var Q8;
            {var subQ3=sQuery(id+"F2.wireOp",EDGE,"E82");var subQ5=sQuery(id+"F2.wireOp",EDGE,"E80");var subQ7=makeQuery(id+"F2.imprint","INTERSECT",VERTEX,{"derivedFrom":[subQ5,subQ3]});Q8=makeQuery(id+"F2.imprint","IMPRINT",FACE,{"disambiguationData":[TD([[makeQuery(id+"F2.imprint","IMPRINT",EDGE,{"disambiguationData":[TD([[subQ7,1.0]])],"derivedFrom":subQ5}),-1.0]])]});}
            var Q9;
            {var subQ0=sQuery(id+"F2.wireOp",EDGE,"E92.MirrorCS");var subQ1=sQuery(id+"F2.wireOp",EDGE,"E90.MirrorC");var subQ2=makeQuery(id+"F2.imprint","INTERSECT",VERTEX,{"derivedFrom":[subQ1,subQ0]});Q9=makeQuery(id+"F2.imprint","IMPRINT",FACE,{"disambiguationData":[TD([[makeQuery(id+"F2.imprint","IMPRINT",EDGE,{"disambiguationData":[TD([[subQ2,1.0]])],"derivedFrom":subQ1}),1.0]])]});}
            var Q10;
            {var subQ1=sQuery(id+"F2.wireOp",EDGE,"E99.MirrorCS");var subQ3=sQuery(id+"F2.wireOp",EDGE,"E116.MirrorC");var subQ4=makeQuery(id+"F2.imprint","INTERSECT",VERTEX,{"derivedFrom":[subQ1,subQ3]});Q10=makeQuery(id+"F2.imprint","IMPRINT",FACE,{"disambiguationData":[TD([[makeQuery(id+"F2.imprint","IMPRINT",EDGE,{"disambiguationData":[TD([[subQ4,-1.0]])],"derivedFrom":subQ3}),-1.0]])]});}
            var Q11;
            {var subQ1=sQuery(id+"F2.wireOp",EDGE,"E103.MirrorCS");var subQ3=sQuery(id+"F2.wireOp",EDGE,"E114.MirrorC");var subQ4=makeQuery(id+"F2.imprint","INTERSECT",VERTEX,{"derivedFrom":[subQ1,subQ3]});Q11=makeQuery(id+"F2.imprint","IMPRINT",FACE,{"disambiguationData":[TD([[makeQuery(id+"F2.imprint","IMPRINT",EDGE,{"disambiguationData":[TD([[subQ4,1.0]])],"derivedFrom":subQ3}),1.0]])]});}
            var Q12;
            {var subQ1=sQuery(id+"F2.wireOp",EDGE,"E77");var subQ6=sQuery(id+"F2.wireOp",EDGE,"E79");var subQ9=makeQuery(id+"F2.imprint","INTERSECT",VERTEX,{"derivedFrom":[subQ1,subQ6]});Q12=makeQuery(id+"F2.imprint","IMPRINT",FACE,{"disambiguationData":[TD([[makeQuery(id+"F2.imprint","IMPRINT",EDGE,{"disambiguationData":[TD([[subQ9,-1.0]])],"derivedFrom":subQ1}),1.0]])]});}
            var Q13;
            {var subQ1=sQuery(id+"F2.wireOp",EDGE,"E77");var subQ6=sQuery(id+"F2.wireOp",EDGE,"E79");var subQ9=makeQuery(id+"F2.imprint","INTERSECT",VERTEX,{"derivedFrom":[subQ1,subQ6]});Q13=makeQuery(id+"F2.imprint","IMPRINT",FACE,{"disambiguationData":[TD([[makeQuery(id+"F2.imprint","IMPRINT",EDGE,{"disambiguationData":[TD([[subQ9,-1.0]])],"derivedFrom":subQ1}),-1.0]])]});}
            var Q14;
            {var subQ0=sQuery(id+"F2.wireOp",EDGE,"E96.MirrorCS");var subQ1=sQuery(id+"F2.wireOp",EDGE,"E90.MirrorC");var subQ2=makeQuery(id+"F2.imprint","INTERSECT",VERTEX,{"derivedFrom":[subQ1,subQ0]});Q14=makeQuery(id+"F2.imprint","IMPRINT",FACE,{"disambiguationData":[TD([[makeQuery(id+"F2.imprint","IMPRINT",EDGE,{"disambiguationData":[TD([[subQ2,1.0]])],"derivedFrom":subQ1}),1.0]])]});}
            var Q15;
            {var subQ0=sQuery(id+"F2.wireOp",EDGE,"E96.MirrorCS");var subQ1=sQuery(id+"F2.wireOp",EDGE,"E90.MirrorC");var subQ2=makeQuery(id+"F2.imprint","INTERSECT",VERTEX,{"derivedFrom":[subQ1,subQ0]});Q15=makeQuery(id+"F2.imprint","IMPRINT",FACE,{"disambiguationData":[TD([[makeQuery(id+"F2.imprint","IMPRINT",EDGE,{"disambiguationData":[TD([[subQ2,-1.0]])],"derivedFrom":subQ1}),1.0]])]});}
            var Q16;
            {var subQ0=sQuery(id+"F2.wireOp",EDGE,"E113.MirrorC");var subQ5=sQuery(id+"F2.wireOp",EDGE,"E112.MirrorCS");var subQ6=makeQuery(id+"F2.imprint","INTERSECT",VERTEX,{"derivedFrom":[subQ5,subQ0]});Q16=makeQuery(id+"F2.imprint","IMPRINT",FACE,{"disambiguationData":[TD([[makeQuery(id+"F2.imprint","IMPRINT",EDGE,{"disambiguationData":[TD([[subQ6,-1.0]])],"derivedFrom":subQ5}),-1.0]])]});}
            var Q17;
            {var subQ3=sQuery(id+"F2.wireOp",EDGE,"E108.MirrorCS");var subQ5=sQuery(id+"F2.wireOp",EDGE,"E115.MirrorC");var subQ6=makeQuery(id+"F2.imprint","INTERSECT",VERTEX,{"derivedFrom":[subQ3,subQ5]});Q17=makeQuery(id+"F2.imprint","IMPRINT",FACE,{"disambiguationData":[TD([[makeQuery(id+"F2.imprint","IMPRINT",EDGE,{"disambiguationData":[TD([[subQ6,-1.0]])],"derivedFrom":subQ3}),-1.0]])]});}
            var Q18;
            {var subQ3=sQuery(id+"F2.wireOp",EDGE,"E108.MirrorCS");var subQ5=sQuery(id+"F2.wireOp",EDGE,"E115.MirrorC");var subQ6=makeQuery(id+"F2.imprint","INTERSECT",VERTEX,{"derivedFrom":[subQ3,subQ5]});Q18=makeQuery(id+"F2.imprint","IMPRINT",FACE,{"disambiguationData":[TD([[makeQuery(id+"F2.imprint","IMPRINT",EDGE,{"disambiguationData":[TD([[subQ6,-1.0]])],"derivedFrom":subQ3}),1.0]])]});}
            var Q19;
            {var subQ0=sQuery(id+"F2.wireOp",EDGE,"E113.MirrorC");var subQ1=sQuery(id+"F2.wireOp",EDGE,"E112.MirrorCS");var subQ2=makeQuery(id+"F2.imprint","INTERSECT",VERTEX,{"derivedFrom":[subQ1,subQ0]});Q19=makeQuery(id+"F2.imprint","IMPRINT",FACE,{"disambiguationData":[TD([[makeQuery(id+"F2.imprint","IMPRINT",EDGE,{"disambiguationData":[TD([[subQ2,-1.0]])],"derivedFrom":subQ1}),1.0]])]});}
            var Q20;
            {var subQ0=sQuery(id+"F2.wireOp",EDGE,"E79");var subQ1=sQuery(id+"F2.wireOp",EDGE,"E77");var subQ2=makeQuery(id+"F2.imprint","INTERSECT",VERTEX,{"derivedFrom":[subQ1,subQ0]});Q20=makeQuery(id+"F2.imprint","IMPRINT",FACE,{"disambiguationData":[TD([[makeQuery(id+"F2.imprint","IMPRINT",EDGE,{"disambiguationData":[TD([[subQ2,1.0]])],"derivedFrom":subQ1}),1.0]])]});}
            var Q21;
            {var subQ0=sQuery(id+"F2.wireOp",EDGE,"E79");var subQ1=sQuery(id+"F2.wireOp",EDGE,"E77");var subQ2=makeQuery(id+"F2.imprint","INTERSECT",VERTEX,{"derivedFrom":[subQ1,subQ0]});Q21=makeQuery(id+"F2.imprint","IMPRINT",FACE,{"disambiguationData":[TD([[makeQuery(id+"F2.imprint","IMPRINT",EDGE,{"disambiguationData":[TD([[subQ2,1.0]])],"derivedFrom":subQ1}),-1.0]])]});}
            var Q22;
            {var subQ0=sQuery(id+"F2.wireOp",EDGE,"E97.MirrorC");var subQ1=sQuery(id+"F2.wireOp",EDGE,"E93.MirrorCS");var subQ2=makeQuery(id+"F2.imprint","INTERSECT",VERTEX,{"derivedFrom":[subQ1,subQ0]});Q22=makeQuery(id+"F2.imprint","IMPRINT",FACE,{"disambiguationData":[TD([[makeQuery(id+"F2.imprint","IMPRINT",EDGE,{"disambiguationData":[TD([[subQ2,1.0]])],"derivedFrom":subQ1}),1.0]])]});}
            var Q23;
            {var subQ0=sQuery(id+"F2.wireOp",EDGE,"E97.MirrorC");var subQ1=sQuery(id+"F2.wireOp",EDGE,"E94.MirrorCS");var subQ2=makeQuery(id+"F2.imprint","INTERSECT",VERTEX,{"derivedFrom":[subQ1,subQ0]});Q23=makeQuery(id+"F2.imprint","IMPRINT",FACE,{"disambiguationData":[TD([[makeQuery(id+"F2.imprint","IMPRINT",EDGE,{"disambiguationData":[TD([[subQ2,-1.0]])],"derivedFrom":subQ1}),1.0]])]});}
            var Q24;
            {var subQ0=sQuery(id+"F2.wireOp",EDGE,"E115.MirrorC");var subQ1=sQuery(id+"F2.wireOp",EDGE,"E108.MirrorCS");var subQ2=makeQuery(id+"F2.imprint","INTERSECT",VERTEX,{"derivedFrom":[subQ1,subQ0]});Q24=makeQuery(id+"F2.imprint","IMPRINT",FACE,{"disambiguationData":[TD([[makeQuery(id+"F2.imprint","IMPRINT",EDGE,{"disambiguationData":[TD([[subQ2,1.0]])],"derivedFrom":subQ1}),-1.0]])]});}
            var Q25;
            {var subQ0=sQuery(id+"F2.wireOp",EDGE,"E115.MirrorC");var subQ1=sQuery(id+"F2.wireOp",EDGE,"E108.MirrorCS");var subQ2=makeQuery(id+"F2.imprint","INTERSECT",VERTEX,{"derivedFrom":[subQ1,subQ0]});Q25=makeQuery(id+"F2.imprint","IMPRINT",FACE,{"disambiguationData":[TD([[makeQuery(id+"F2.imprint","IMPRINT",EDGE,{"disambiguationData":[TD([[subQ2,1.0]])],"derivedFrom":subQ1}),1.0]])]});}
            var Q26;
            {var subQ0=sQuery(id+"F2.wireOp",EDGE,"E113.MirrorC");var subQ1=sQuery(id+"F2.wireOp",EDGE,"E110.MirrorCS");var subQ2=makeQuery(id+"F2.imprint","INTERSECT",VERTEX,{"derivedFrom":[subQ1,subQ0]});Q26=makeQuery(id+"F2.imprint","IMPRINT",FACE,{"disambiguationData":[TD([[makeQuery(id+"F2.imprint","IMPRINT",EDGE,{"disambiguationData":[TD([[subQ2,-1.0]])],"derivedFrom":subQ1}),-1.0]])]});}
            var Q27;
            {var subQ0=sQuery(id+"F2.wireOp",EDGE,"E113.MirrorC");var subQ1=sQuery(id+"F2.wireOp",EDGE,"E112.MirrorCS");var subQ2=makeQuery(id+"F2.imprint","INTERSECT",VERTEX,{"derivedFrom":[subQ1,subQ0]});Q27=makeQuery(id+"F2.imprint","IMPRINT",FACE,{"disambiguationData":[TD([[makeQuery(id+"F2.imprint","IMPRINT",EDGE,{"disambiguationData":[TD([[subQ2,1.0]])],"derivedFrom":subQ1}),1.0]])]});}
            var Q28;
            {var subQ4=makeQuery(id+"F1.opExtrude","CAP_EDGE",EDGE,{"disambiguationData":[OSD([sQuery(id+"F0.wireOp",EDGE,"E9.MirrorC")])],"isStart":false});var subQ7=sQuery(id+"F2.wireOp",EDGE,"E77");var subQ8=makeQuery(id+"F2.imprint","INTERSECT",VERTEX,{"derivedFrom":[subQ4,subQ7]});Q28=makeQuery(id+"F2.imprint","IMPRINT",FACE,{"disambiguationData":[TD([[makeQuery(id+"F2.imprint","IMPRINT",EDGE,{"disambiguationData":[TD([[subQ8,-1.0]])],"derivedFrom":subQ7}),1.0]])]});}
            var Q29;
            {var subQ3=sQuery(id+"F2.wireOp",EDGE,"E77");var subQ7=makeQuery(id+"F1.opExtrude","CAP_EDGE",EDGE,{"disambiguationData":[OSD([sQuery(id+"F0.wireOp",EDGE,"E9.MirrorC")])],"isStart":false});var subQ9=makeQuery(id+"F2.imprint","INTERSECT",VERTEX,{"derivedFrom":[subQ7,subQ3]});Q29=makeQuery(id+"F2.imprint","IMPRINT",FACE,{"disambiguationData":[TD([[makeQuery(id+"F2.imprint","IMPRINT",EDGE,{"disambiguationData":[TD([[subQ9,-1.0]])],"derivedFrom":subQ3}),-1.0]])]});}
            var Q30;
            {var subQ3=sQuery(id+"F2.wireOp",EDGE,"E96.MirrorCS");var subQ5=makeQuery(id+"F1.opExtrude","CAP_EDGE",EDGE,{"disambiguationData":[OSD([sQuery(id+"F0.wireOp",EDGE,"E7.MirrorC")])],"isStart":false});var subQ6=makeQuery(id+"F2.imprint","INTERSECT",VERTEX,{"derivedFrom":[subQ5,subQ3]});Q30=makeQuery(id+"F2.imprint","IMPRINT",FACE,{"disambiguationData":[TD([[makeQuery(id+"F2.imprint","IMPRINT",EDGE,{"disambiguationData":[TD([[subQ6,-1.0]])],"derivedFrom":subQ3}),1.0]])]});}
            var Q31;
            {var subQ0=sQuery(id+"F2.wireOp",EDGE,"E96.MirrorCS");var subQ1=makeQuery(id+"F1.opExtrude","CAP_EDGE",EDGE,{"disambiguationData":[OSD([sQuery(id+"F0.wireOp",EDGE,"E7.MirrorC")])],"isStart":false});var subQ2=makeQuery(id+"F2.imprint","INTERSECT",VERTEX,{"derivedFrom":[subQ1,subQ0]});Q31=makeQuery(id+"F2.imprint","IMPRINT",FACE,{"disambiguationData":[TD([[makeQuery(id+"F2.imprint","IMPRINT",EDGE,{"disambiguationData":[TD([[subQ2,-1.0]])],"derivedFrom":subQ0}),-1.0]])]});}
            var Q32;
            {var subQ0=sQuery(id+"F2.wireOp",EDGE,"E112.MirrorCS");var subQ1=makeQuery(id+"F1.opExtrude","CAP_EDGE",EDGE,{"disambiguationData":[OSD([sQuery(id+"F0.wireOp",EDGE,"E3")])],"isStart":false});var subQ2=makeQuery(id+"F2.imprint","INTERSECT",VERTEX,{"derivedFrom":[subQ1,subQ0]});Q32=makeQuery(id+"F2.imprint","IMPRINT",FACE,{"disambiguationData":[TD([[makeQuery(id+"F2.imprint","IMPRINT",EDGE,{"disambiguationData":[TD([[subQ2,-1.0]])],"derivedFrom":subQ0}),-1.0]])]});}
            var Q33;
            {var subQ3=sQuery(id+"F2.wireOp",EDGE,"E108.MirrorCS");var subQ5=makeQuery(id+"F1.opExtrude","CAP_EDGE",EDGE,{"disambiguationData":[OSD([sQuery(id+"F0.wireOp",EDGE,"E5.MirrorC")])],"isStart":false});var subQ6=makeQuery(id+"F2.imprint","INTERSECT",VERTEX,{"derivedFrom":[subQ5,subQ3]});Q33=makeQuery(id+"F2.imprint","IMPRINT",FACE,{"disambiguationData":[TD([[makeQuery(id+"F2.imprint","IMPRINT",EDGE,{"disambiguationData":[TD([[subQ6,-1.0]])],"derivedFrom":subQ3}),-1.0]])]});}
            var Q34;
            {var subQ3=sQuery(id+"F2.wireOp",EDGE,"E108.MirrorCS");var subQ5=makeQuery(id+"F1.opExtrude","CAP_EDGE",EDGE,{"disambiguationData":[OSD([sQuery(id+"F0.wireOp",EDGE,"E5.MirrorC")])],"isStart":false});var subQ6=makeQuery(id+"F2.imprint","INTERSECT",VERTEX,{"derivedFrom":[subQ5,subQ3]});Q34=makeQuery(id+"F2.imprint","IMPRINT",FACE,{"disambiguationData":[TD([[makeQuery(id+"F2.imprint","IMPRINT",EDGE,{"disambiguationData":[TD([[subQ6,-1.0]])],"derivedFrom":subQ3}),1.0]])]});}
            var Q35;
            {var subQ3=sQuery(id+"F2.wireOp",EDGE,"E112.MirrorCS");var subQ7=makeQuery(id+"F1.opExtrude","CAP_EDGE",EDGE,{"disambiguationData":[OSD([sQuery(id+"F0.wireOp",EDGE,"E3")])],"isStart":false});var subQ8=makeQuery(id+"F2.imprint","INTERSECT",VERTEX,{"derivedFrom":[subQ7,subQ3]});Q35=makeQuery(id+"F2.imprint","IMPRINT",FACE,{"disambiguationData":[TD([[makeQuery(id+"F2.imprint","IMPRINT",EDGE,{"disambiguationData":[TD([[subQ8,-1.0]])],"derivedFrom":subQ3}),1.0]])]});}
            extrude(context, id + "F3", {"entities" : qUnion([Q0, Q1, Q2, Q3, Q4, Q5, Q6, Q7, Q8, Q9, Q10, Q11, Q12, Q13, Q14, Q15, Q16, Q17, Q18, Q19, Q20, Q21, Q22, Q23, Q24, Q25, Q26, Q27, Q28, Q29, Q30, Q31, Q32, Q33, Q34, Q35]), "operationType" : NewBodyOperationType.ADD, "oppositeDirection" : true, "depth" : 3.17 * mm});
        }
        {
            var Q0;
            {var subQ0=sQuery(id+"F0.wireOp",EDGE,"E5.MirrorC");var subQ1=sQuery(id+"F0.wireOp",EDGE,"E3");var subQ2=sQuery(id+"F0.wireOp",EDGE,"E7.MirrorC");var subQ3=sQuery(id+"F0.wireOp",EDGE,"E9.MirrorC");Q0=makeQuery(id+"F3.boolean.opBoolean","MERGE",FACE,{"derivedFrom":[makeQuery(id+"F1.opExtrude","CAP_FACE",FACE,{"disambiguationData":[OSD([sQuery(id+"F0.wireOp",EDGE,"E1.bottom"),sQuery(id+"F0.wireOp",EDGE,"E1.left"),sQuery(id+"F0.wireOp",EDGE,"E1.right"),sQuery(id+"F0.wireOp",EDGE,"E2"),subQ1,sQuery(id+"F0.wireOp",EDGE,"E4.MirrorC"),subQ0,sQuery(id+"F0.wireOp",EDGE,"E6.MirrorC"),subQ2,sQuery(id+"F0.wireOp",EDGE,"E8.MirrorC"),subQ3,sQuery(id+"F0.wireOp",EDGE,"E11"),sQuery(id+"F0.wireOp",EDGE,"E13.MirrorCS"),sQuery(id+"F0.wireOp",EDGE,"E14.MirrorCS"),sQuery(id+"F0.wireOp",EDGE,"E15.MirrorCS"),sQuery(id+"F0.wireOp",EDGE,"E16.0"),sQuery(id+"F0.wireOp",EDGE,"E16.1"),sQuery(id+"F0.wireOp",EDGE,"E16.2"),sQuery(id+"F0.wireOp",EDGE,"E16.3"),sQuery(id+"F0.wireOp",EDGE,"E17.right"),sQuery(id+"F0.wireOp",EDGE,"E18.MirrorCS"),sQuery(id+"F0.wireOp",EDGE,"E22.MirrorCS"),sQuery(id+"F0.wireOp",EDGE,"E23.MirrorCS"),sQuery(id+"F0.wireOp",EDGE,"E24.MirrorCS"),sQuery(id+"F0.wireOp",EDGE,"E26.top"),sQuery(id+"F0.wireOp",EDGE,"E27.MirrorCS"),sQuery(id+"F0.wireOp",EDGE,"E31.MirrorCS"),sQuery(id+"F0.wireOp",EDGE,"E32.MirrorCS"),sQuery(id+"F0.wireOp",EDGE,"E36"),sQuery(id+"F0.wireOp",EDGE,"E38"),sQuery(id+"F0.wireOp",EDGE,"E39.MirrorCS"),sQuery(id+"F0.wireOp",EDGE,"E41.MirrorCS"),sQuery(id+"F0.wireOp",EDGE,"E43.MirrorCS"),sQuery(id+"F0.wireOp",EDGE,"E45.MirrorCS"),sQuery(id+"F0.wireOp",EDGE,"E47.MirrorCS"),sQuery(id+"F0.wireOp",EDGE,"E49.MirrorCS")])],"isStart":false}),makeQuery(id+"F3.opExtrude","CAP_FACE",FACE,{"disambiguationData":[OSD([subQ3,sQuery(id+"F2.wireOp",EDGE,"E79"),sQuery(id+"F2.wireOp",EDGE,"E80"),sQuery(id+"F2.wireOp",EDGE,"E83"),sQuery(id+"F2.wireOp",EDGE,"E84"),sQuery(id+"F2.wireOp",EDGE,"E85"),sQuery(id+"F2.wireOp",EDGE,"E86")])],"isStart":true}),makeQuery(id+"F3.opExtrude","CAP_FACE",FACE,{"disambiguationData":[OSD([subQ2,sQuery(id+"F2.wireOp",EDGE,"E87.MirrorCS"),sQuery(id+"F2.wireOp",EDGE,"E88.MirrorCS"),sQuery(id+"F2.wireOp",EDGE,"E90.MirrorC"),sQuery(id+"F2.wireOp",EDGE,"E93.MirrorCS"),sQuery(id+"F2.wireOp",EDGE,"E94.MirrorCS"),sQuery(id+"F2.wireOp",EDGE,"E97.MirrorC")])],"isStart":true}),makeQuery(id+"F3.opExtrude","CAP_FACE",FACE,{"disambiguationData":[OSD([subQ1,sQuery(id+"F2.wireOp",EDGE,"E98.MirrorCS"),sQuery(id+"F2.wireOp",EDGE,"E102.MirrorCS"),sQuery(id+"F2.wireOp",EDGE,"E110.MirrorCS"),sQuery(id+"F2.wireOp",EDGE,"E113.MirrorC"),sQuery(id+"F2.wireOp",EDGE,"E116.MirrorC"),sQuery(id+"F2.wireOp",EDGE,"E117.MirrorCS")])],"isStart":true}),makeQuery(id+"F3.opExtrude","CAP_FACE",FACE,{"disambiguationData":[OSD([subQ0,sQuery(id+"F2.wireOp",EDGE,"E100.MirrorCS"),sQuery(id+"F2.wireOp",EDGE,"E101.MirrorCS"),sQuery(id+"F2.wireOp",EDGE,"E114.MirrorC"),sQuery(id+"F2.wireOp",EDGE,"E115.MirrorC"),sQuery(id+"F2.wireOp",EDGE,"E118.MirrorCS"),sQuery(id+"F2.wireOp",EDGE,"E119.MirrorCS")])],"isStart":true})]});}
            var sketch = newSketch(context, id + "F4", { "sketchPlane" : qUnion([Q0])});
            skLineSegment(sketch, "E120", {"start": v(-32.7, -32.33) * mm, "end": v(-30.46, -30.08) * mm});
            skLineSegment(sketch, "E121", {"start": v(-32.7, -32.33) * mm, "end": v(-32.7, -29.15) * mm});
            skLineSegment(sketch, "E122", {"start": v(-19.05, -19.05) * mm, "end": v(-20.22, -20.22) * mm});
            skLineSegment(sketch, "E123", {"start": v(-19.05, -19.05) * mm, "end": v(-19.05, -17.4) * mm});
            skLineSegment(sketch, "E124", {"start": v(-30.46, -30.08) * mm, "end": v(-20.22, -20.22) * mm});
            skPoint(sketch, "E125", {"position": v(-29.32, -28.98) * mm});
            skPoint(sketch, "E126", {"position": v(-21.36, -21.32) * mm});
            skCircle(sketch, "E127", {"center": v(-28.18, -27.88) * mm, "radius": 1.59 * mm});
            skPoint(sketch, "E127.second.point", {"position": v(-27.03, -26.78) * mm});
            skPoint(sketch, "E127.third.point", {"position": v(-29.07, -26.57) * mm});
            skCircle(sketch, "E128", {"center": v(-22.5, -22.42) * mm, "radius": 1.59 * mm});
            skPoint(sketch, "E128.second.point", {"position": v(-23.65, -23.52) * mm});
            skPoint(sketch, "E128.third.point", {"position": v(-21.36, -23.52) * mm});
            skLineSegment(sketch, "E129", {"start": v(-28.18, -27.88) * mm, "end": v(-27.08, -29.03) * mm});
            skLineSegment(sketch, "E130", {"start": v(-28.18, -27.88) * mm, "end": v(-29.28, -26.74) * mm});
            skLineSegment(sketch, "E131", {"start": v(-22.5, -22.42) * mm, "end": v(-23.6, -21.28) * mm});
            skLineSegment(sketch, "E132", {"start": v(-22.5, -22.42) * mm, "end": v(-21.4, -23.56) * mm});
            skArc(sketch, "E133", {"start": v(-21.4, -23.56) * mm, "mid": v(-24.35, -26.18) * mm, "end": v(-27.08, -29.03) * mm});
            skArc(sketch, "E134", {"start": v(-29.28, -26.74) * mm, "mid": v(-26.34, -24.12) * mm, "end": v(-23.6, -21.28) * mm});
            skLineSegment(sketch, "E135.MirrorCS", {"start": v(-22.5, 22.42) * mm, "end": v(-23.6, 21.28) * mm});
            skLineSegment(sketch, "E136.MirrorCS", {"start": v(-22.5, 22.42) * mm, "end": v(-21.4, 23.56) * mm});
            skLineSegment(sketch, "E137.MirrorCS", {"start": v(-28.18, 27.88) * mm, "end": v(-29.28, 26.74) * mm});
            skLineSegment(sketch, "E138.MirrorCS", {"start": v(-28.18, 27.88) * mm, "end": v(-27.08, 29.03) * mm});
            skLineSegment(sketch, "E139.MirrorCS", {"start": v(-19.05, 19.05) * mm, "end": v(-20.22, 20.22) * mm});
            skLineSegment(sketch, "E140.MirrorCS", {"start": v(-32.7, 32.33) * mm, "end": v(-30.46, 30.08) * mm});
            skLineSegment(sketch, "E141.MirrorCS", {"start": v(-32.7, 32.33) * mm, "end": v(-32.7, 29.15) * mm});
            skCircle(sketch, "E142.MirrorC", {"center": v(-22.5, 22.42) * mm, "radius": 1.59 * mm});
            skCircle(sketch, "E143.MirrorC", {"center": v(-28.18, 27.88) * mm, "radius": 1.59 * mm});
            skLineSegment(sketch, "E144.MirrorCS", {"start": v(-30.46, 30.08) * mm, "end": v(-20.22, 20.22) * mm});
            skLineSegment(sketch, "E145.MirrorCS", {"start": v(-19.05, 19.05) * mm, "end": v(-19.05, 17.4) * mm});
            skPoint(sketch, "E146.MirrorP", {"position": v(-29.32, 28.98) * mm});
            skPoint(sketch, "E147.MirrorP", {"position": v(-27.03, 26.78) * mm});
            skPoint(sketch, "E148.MirrorP", {"position": v(-29.07, 26.57) * mm});
            skPoint(sketch, "E149.MirrorP", {"position": v(-23.65, 23.52) * mm});
            skPoint(sketch, "E150.MirrorP", {"position": v(-21.36, 23.52) * mm});
            skPoint(sketch, "E151.MirrorP", {"position": v(-21.36, 21.32) * mm});
            skArc(sketch, "E152.MirrorCS", {"start": v(-29.28, 26.74) * mm, "mid": v(-26.34, 24.12) * mm, "end": v(-23.6, 21.28) * mm});
            skArc(sketch, "E153.MirrorCS", {"start": v(-21.4, 23.56) * mm, "mid": v(-24.35, 26.18) * mm, "end": v(-27.08, 29.03) * mm});
            skLineSegment(sketch, "E154.MirrorCS", {"start": v(22.5, -22.42) * mm, "end": v(21.4, -23.56) * mm});
            skLineSegment(sketch, "E155.MirrorCS", {"start": v(22.5, -22.42) * mm, "end": v(23.6, -21.28) * mm});
            skLineSegment(sketch, "E156.MirrorCS", {"start": v(28.18, -27.88) * mm, "end": v(29.28, -26.74) * mm});
            skLineSegment(sketch, "E157.MirrorCS", {"start": v(28.18, -27.88) * mm, "end": v(27.08, -29.03) * mm});
            skLineSegment(sketch, "E158.MirrorCS", {"start": v(19.05, -19.05) * mm, "end": v(20.22, -20.22) * mm});
            skLineSegment(sketch, "E159.MirrorCS", {"start": v(28.18, 27.88) * mm, "end": v(29.28, 26.74) * mm});
            skLineSegment(sketch, "E160.MirrorCS", {"start": v(22.5, 22.42) * mm, "end": v(21.4, 23.56) * mm});
            skLineSegment(sketch, "E161.MirrorCS", {"start": v(28.18, 27.88) * mm, "end": v(27.08, 29.03) * mm});
            skLineSegment(sketch, "E162.MirrorCS", {"start": v(22.5, 22.42) * mm, "end": v(23.6, 21.28) * mm});
            skCircle(sketch, "E163.MirrorC", {"center": v(28.18, 27.88) * mm, "radius": 1.59 * mm});
            skCircle(sketch, "E164.MirrorC", {"center": v(22.5, -22.42) * mm, "radius": 1.59 * mm});
            skLineSegment(sketch, "E165.MirrorCS", {"start": v(32.7, -32.33) * mm, "end": v(30.46, -30.08) * mm});
            skLineSegment(sketch, "E166.MirrorCS", {"start": v(19.05, 19.05) * mm, "end": v(19.05, 17.4) * mm});
            skLineSegment(sketch, "E167.MirrorCS", {"start": v(19.05, 19.05) * mm, "end": v(20.22, 20.22) * mm});
            skLineSegment(sketch, "E168.MirrorCS", {"start": v(32.7, 32.33) * mm, "end": v(30.46, 30.08) * mm});
            skCircle(sketch, "E169.MirrorC", {"center": v(28.18, -27.88) * mm, "radius": 1.59 * mm});
            skLineSegment(sketch, "E170.MirrorCS", {"start": v(30.46, -30.08) * mm, "end": v(20.22, -20.22) * mm});
            skLineSegment(sketch, "E171.MirrorCS", {"start": v(19.05, -19.05) * mm, "end": v(19.05, -17.4) * mm});
            skLineSegment(sketch, "E172.MirrorCS", {"start": v(32.7, -32.33) * mm, "end": v(32.7, -29.15) * mm});
            skCircle(sketch, "E173.MirrorC", {"center": v(22.5, 22.42) * mm, "radius": 1.59 * mm});
            skLineSegment(sketch, "E174.MirrorCS", {"start": v(30.46, 30.08) * mm, "end": v(20.22, 20.22) * mm});
            skLineSegment(sketch, "E175.MirrorCS", {"start": v(32.7, 32.33) * mm, "end": v(32.7, 29.15) * mm});
            skPoint(sketch, "E176.MirrorP", {"position": v(27.03, -26.78) * mm});
            skPoint(sketch, "E177.MirrorP", {"position": v(29.32, -28.98) * mm});
            skPoint(sketch, "E178.MirrorP", {"position": v(21.36, 23.52) * mm});
            skArc(sketch, "E179.MirrorCS", {"start": v(29.28, -26.74) * mm, "mid": v(26.34, -24.12) * mm, "end": v(23.6, -21.28) * mm});
            skArc(sketch, "E180.MirrorCS", {"start": v(21.4, -23.56) * mm, "mid": v(24.35, -26.18) * mm, "end": v(27.08, -29.03) * mm});
            skPoint(sketch, "E181.MirrorP", {"position": v(23.65, 23.52) * mm});
            skPoint(sketch, "E182.MirrorP", {"position": v(21.36, -21.32) * mm});
            skPoint(sketch, "E183.MirrorP", {"position": v(21.36, 21.32) * mm});
            skArc(sketch, "E184.MirrorCS", {"start": v(29.28, 26.74) * mm, "mid": v(26.34, 24.12) * mm, "end": v(23.6, 21.28) * mm});
            skPoint(sketch, "E185.MirrorP", {"position": v(29.07, 26.57) * mm});
            skPoint(sketch, "E186.MirrorP", {"position": v(29.07, -26.57) * mm});
            skPoint(sketch, "E187.MirrorP", {"position": v(29.32, 28.98) * mm});
            skPoint(sketch, "E188.MirrorP", {"position": v(23.65, -23.52) * mm});
            skArc(sketch, "E189.MirrorCS", {"start": v(21.4, 23.56) * mm, "mid": v(24.35, 26.18) * mm, "end": v(27.08, 29.03) * mm});
            skPoint(sketch, "E190.MirrorP", {"position": v(27.03, 26.78) * mm});
            skPoint(sketch, "E191.MirrorP", {"position": v(21.36, -23.52) * mm});
            skSolve(sketch);
        }
        {
            var Q0;
            Q0=qSketchRegion(id+"F4",true);
            extrude(context, id + "F5", {"entities" : qUnion([Q0]), "operationType" : NewBodyOperationType.REMOVE, "oppositeDirection" : true, "depth" : 25.4 * mm});
        }
        {
            var Q0;
            {var subQ0=sQuery(id+"F2.wireOp",EDGE,"E96.MirrorCS");var subQ1=sQuery(id+"F2.wireOp",EDGE,"E90.MirrorC");var subQ2=makeQuery(id+"F2.imprint","INTERSECT",VERTEX,{"derivedFrom":[subQ1,subQ0]});Q0=makeQuery(id+"F2.imprint","IMPRINT",FACE,{"disambiguationData":[TD([[makeQuery(id+"F2.imprint","IMPRINT",EDGE,{"disambiguationData":[TD([[subQ2,-1.0]])],"derivedFrom":subQ1}),1.0]])]});}
            var Q1;
            {var subQ0=sQuery(id+"F2.wireOp",EDGE,"E96.MirrorCS");var subQ1=sQuery(id+"F2.wireOp",EDGE,"E90.MirrorC");var subQ2=makeQuery(id+"F2.imprint","INTERSECT",VERTEX,{"derivedFrom":[subQ1,subQ0]});Q1=makeQuery(id+"F2.imprint","IMPRINT",FACE,{"disambiguationData":[TD([[makeQuery(id+"F2.imprint","IMPRINT",EDGE,{"disambiguationData":[TD([[subQ2,1.0]])],"derivedFrom":subQ1}),1.0]])]});}
            var Q2;
            {var subQ0=sQuery(id+"F2.wireOp",EDGE,"E92.MirrorCS");var subQ1=sQuery(id+"F2.wireOp",EDGE,"E90.MirrorC");var subQ2=makeQuery(id+"F2.imprint","INTERSECT",VERTEX,{"derivedFrom":[subQ1,subQ0]});Q2=makeQuery(id+"F2.imprint","IMPRINT",FACE,{"disambiguationData":[TD([[makeQuery(id+"F2.imprint","IMPRINT",EDGE,{"disambiguationData":[TD([[subQ2,1.0]])],"derivedFrom":subQ1}),1.0]])]});}
            var Q3;
            {var subQ1=sQuery(id+"F2.wireOp",EDGE,"E103.MirrorCS");var subQ3=sQuery(id+"F2.wireOp",EDGE,"E114.MirrorC");var subQ4=makeQuery(id+"F2.imprint","INTERSECT",VERTEX,{"derivedFrom":[subQ1,subQ3]});Q3=makeQuery(id+"F2.imprint","IMPRINT",FACE,{"disambiguationData":[TD([[makeQuery(id+"F2.imprint","IMPRINT",EDGE,{"disambiguationData":[TD([[subQ4,1.0]])],"derivedFrom":subQ3}),1.0]])]});}
            var Q4;
            {var subQ3=sQuery(id+"F2.wireOp",EDGE,"E108.MirrorCS");var subQ5=sQuery(id+"F2.wireOp",EDGE,"E115.MirrorC");var subQ6=makeQuery(id+"F2.imprint","INTERSECT",VERTEX,{"derivedFrom":[subQ3,subQ5]});Q4=makeQuery(id+"F2.imprint","IMPRINT",FACE,{"disambiguationData":[TD([[makeQuery(id+"F2.imprint","IMPRINT",EDGE,{"disambiguationData":[TD([[subQ6,-1.0]])],"derivedFrom":subQ3}),1.0]])]});}
            var Q5;
            {var subQ3=sQuery(id+"F2.wireOp",EDGE,"E108.MirrorCS");var subQ5=sQuery(id+"F2.wireOp",EDGE,"E115.MirrorC");var subQ6=makeQuery(id+"F2.imprint","INTERSECT",VERTEX,{"derivedFrom":[subQ3,subQ5]});Q5=makeQuery(id+"F2.imprint","IMPRINT",FACE,{"disambiguationData":[TD([[makeQuery(id+"F2.imprint","IMPRINT",EDGE,{"disambiguationData":[TD([[subQ6,-1.0]])],"derivedFrom":subQ3}),-1.0]])]});}
            var Q6;
            {var subQ0=sQuery(id+"F2.wireOp",EDGE,"E113.MirrorC");var subQ5=sQuery(id+"F2.wireOp",EDGE,"E112.MirrorCS");var subQ6=makeQuery(id+"F2.imprint","INTERSECT",VERTEX,{"derivedFrom":[subQ5,subQ0]});Q6=makeQuery(id+"F2.imprint","IMPRINT",FACE,{"disambiguationData":[TD([[makeQuery(id+"F2.imprint","IMPRINT",EDGE,{"disambiguationData":[TD([[subQ6,-1.0]])],"derivedFrom":subQ5}),-1.0]])]});}
            var Q7;
            {var subQ1=sQuery(id+"F2.wireOp",EDGE,"E99.MirrorCS");var subQ3=sQuery(id+"F2.wireOp",EDGE,"E116.MirrorC");var subQ4=makeQuery(id+"F2.imprint","INTERSECT",VERTEX,{"derivedFrom":[subQ1,subQ3]});Q7=makeQuery(id+"F2.imprint","IMPRINT",FACE,{"disambiguationData":[TD([[makeQuery(id+"F2.imprint","IMPRINT",EDGE,{"disambiguationData":[TD([[subQ4,-1.0]])],"derivedFrom":subQ3}),-1.0]])]});}
            var Q8;
            {var subQ0=sQuery(id+"F2.wireOp",EDGE,"E113.MirrorC");var subQ1=sQuery(id+"F2.wireOp",EDGE,"E112.MirrorCS");var subQ2=makeQuery(id+"F2.imprint","INTERSECT",VERTEX,{"derivedFrom":[subQ1,subQ0]});Q8=makeQuery(id+"F2.imprint","IMPRINT",FACE,{"disambiguationData":[TD([[makeQuery(id+"F2.imprint","IMPRINT",EDGE,{"disambiguationData":[TD([[subQ2,-1.0]])],"derivedFrom":subQ1}),1.0]])]});}
            var Q9;
            {var subQ3=sQuery(id+"F2.wireOp",EDGE,"E82");var subQ5=sQuery(id+"F2.wireOp",EDGE,"E80");var subQ7=makeQuery(id+"F2.imprint","INTERSECT",VERTEX,{"derivedFrom":[subQ5,subQ3]});Q9=makeQuery(id+"F2.imprint","IMPRINT",FACE,{"disambiguationData":[TD([[makeQuery(id+"F2.imprint","IMPRINT",EDGE,{"disambiguationData":[TD([[subQ7,1.0]])],"derivedFrom":subQ5}),-1.0]])]});}
            var Q10;
            {var subQ1=sQuery(id+"F2.wireOp",EDGE,"E77");var subQ6=sQuery(id+"F2.wireOp",EDGE,"E79");var subQ9=makeQuery(id+"F2.imprint","INTERSECT",VERTEX,{"derivedFrom":[subQ1,subQ6]});Q10=makeQuery(id+"F2.imprint","IMPRINT",FACE,{"disambiguationData":[TD([[makeQuery(id+"F2.imprint","IMPRINT",EDGE,{"disambiguationData":[TD([[subQ9,-1.0]])],"derivedFrom":subQ1}),1.0]])]});}
            var Q11;
            {var subQ1=sQuery(id+"F2.wireOp",EDGE,"E77");var subQ6=sQuery(id+"F2.wireOp",EDGE,"E79");var subQ9=makeQuery(id+"F2.imprint","INTERSECT",VERTEX,{"derivedFrom":[subQ1,subQ6]});Q11=makeQuery(id+"F2.imprint","IMPRINT",FACE,{"disambiguationData":[TD([[makeQuery(id+"F2.imprint","IMPRINT",EDGE,{"disambiguationData":[TD([[subQ9,-1.0]])],"derivedFrom":subQ1}),-1.0]])]});}
            extrude(context, id + "F6", {"entities" : qUnion([Q0, Q1, Q2, Q3, Q4, Q5, Q6, Q7, Q8, Q9, Q10, Q11]), "operationType" : NewBodyOperationType.ADD, "depth" : 9.52 * mm});
        }
        {
            var Q0;
            {var subQ5=makeQuery(id+"F1.opExtrude","CAP_EDGE",EDGE,{"disambiguationData":[OSD([sQuery(id+"F0.wireOp",EDGE,"E11")])],"isStart":false});Q0=makeQuery(id+"F2.imprint","IMPRINT",FACE,{"disambiguationData":[TD([[makeQuery(id+"F2.imprint","IMPRINT",EDGE,{"derivedFrom":subQ5}),-1.0]])]});}
            var sketch = newSketch(context, id + "F7", { "sketchPlane" : qUnion([Q0])});
            skCircle(sketch, "E192", {"center": v(0, 0) * mm, "radius": 6.35 * mm});
            skSolve(sketch);
        }
        {
            var Q0;
            Q0=qSketchRegion(id+"F7",true);
            extrude(context, id + "F8", {"entities" : qUnion([Q0]), "operationType" : NewBodyOperationType.REMOVE, "oppositeDirection" : true, "depth" : 25.4 * mm});
        }
    });
